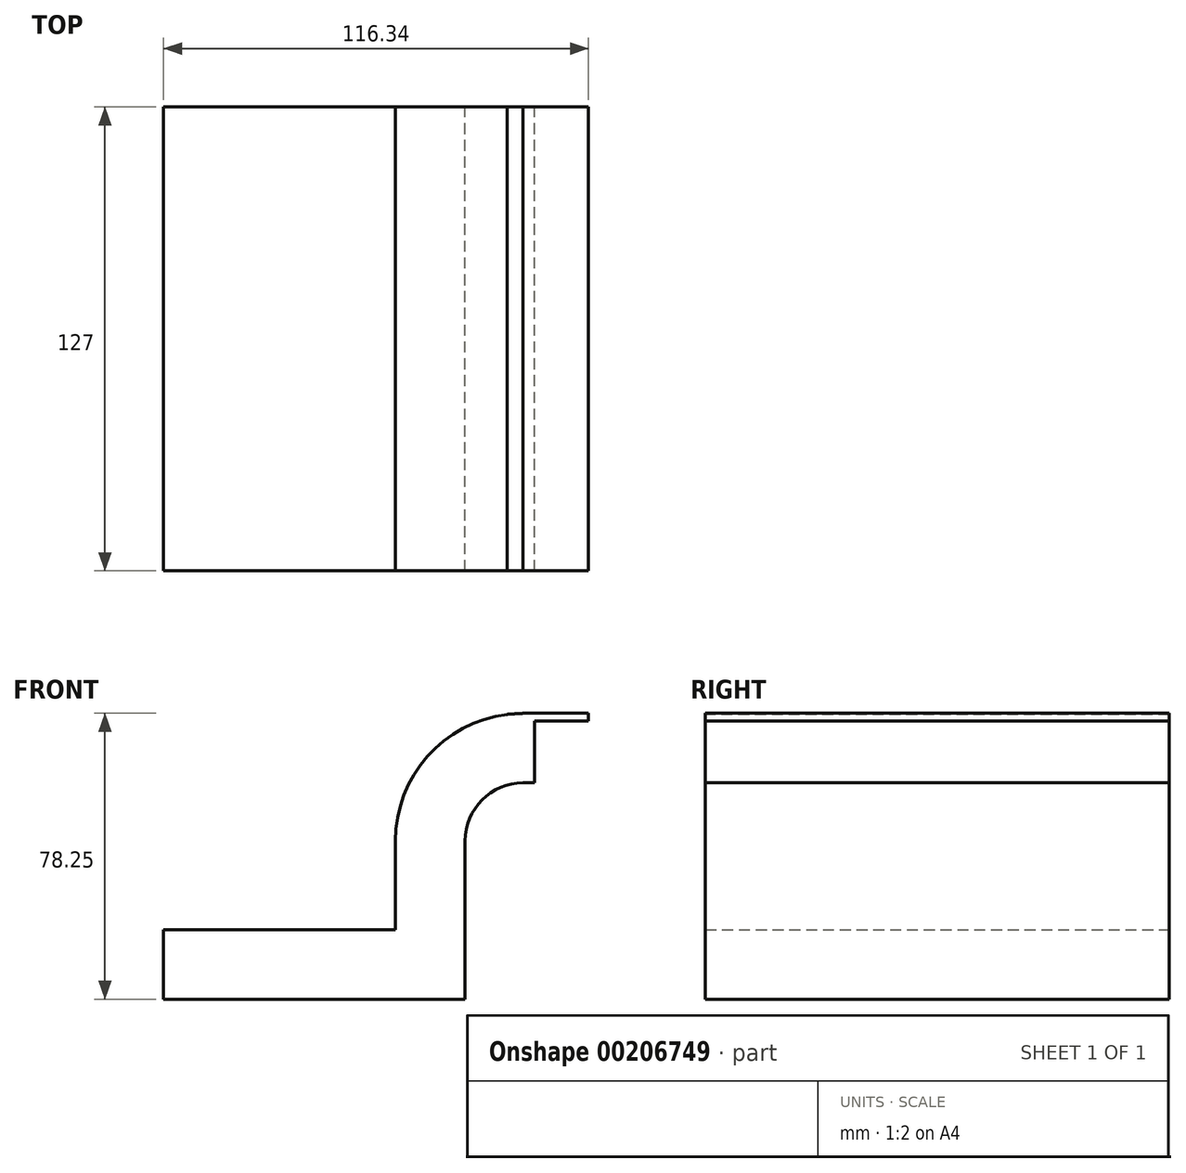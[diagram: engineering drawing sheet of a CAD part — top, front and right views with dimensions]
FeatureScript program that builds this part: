
annotation { "Feature Type Name" : "Feature", "Feature Type Description" : "" }
export const myFeature = defineFeature(function(context is Context, id is Id, definition is map)
    precondition{}
    {
        {
            var Q0;
            Q0=qCreatedBy(makeId("Front.planeOp"),FACE);
            var sketch = newSketch(context, id + "F0", { "sketchPlane" : qUnion([Q0])});
            skLineSegment(sketch, "E0.bottom", {"start": v(-41.28, -9.53) * mm, "end": v(41.28, -9.53) * mm});
            skLineSegment(sketch, "E0.top", {"start": v(-41.28, 9.53) * mm, "end": v(41.28, 9.53) * mm});
            skLineSegment(sketch, "E0.left", {"start": v(-41.28, -9.53) * mm, "end": v(-41.28, 9.53) * mm});
            skLineSegment(sketch, "E0.right", {"start": v(41.28, -9.53) * mm, "end": v(41.28, 9.52) * mm});
            skPoint(sketch, "E0.middle", {"position": v(0, 0) * mm});
            skLineSegment(sketch, "E1.bottom", {"start": v(111.12, 38.1) * mm, "end": v(60.32, 38.1) * mm});
            skLineSegment(sketch, "E1.top", {"start": v(111.12, 66.68) * mm, "end": v(60.32, 66.68) * mm});
            skLineSegment(sketch, "E1.left", {"start": v(111.12, 38.1) * mm, "end": v(111.12, 66.68) * mm});
            skLineSegment(sketch, "E1.right", {"start": v(60.32, 38.1) * mm, "end": v(60.32, 66.68) * mm});
            skPoint(sketch, "E1.middle", {"position": v(85.72, 52.39) * mm});
            skLineSegment(sketch, "E2", {"start": v(41.28, 9.52) * mm, "end": v(41.28, 33.8) * mm});
            skArc(sketch, "E3", {"start": v(41.27, 33.8) * mm, "mid": v(45.92, 45.02) * mm, "end": v(57.15, 49.67) * mm});
            skLineSegment(sketch, "E4", {"start": v(57.15, 49.67) * mm, "end": v(75.07, 49.67) * mm});
            skLineSegment(sketch, "E5.0", {"start": v(57.15, 68.72) * mm, "end": v(75.07, 68.72) * mm});
            skArc(sketch, "E5.1", {"start": v(22.22, 33.8) * mm, "mid": v(32.45, 58.5) * mm, "end": v(57.15, 68.72) * mm});
            skLineSegment(sketch, "E5.2", {"start": v(22.22, 9.52) * mm, "end": v(22.22, 33.8) * mm});
            skLineSegment(sketch, "E6", {"start": v(75.07, 49.67) * mm, "end": v(75.07, 68.72) * mm});
            skFitSpline(sketch, "E7", {"points": [v(57.15, 68.72) * mm, v(-41.28, 9.52) * mm], "startDerivative": vector(-206.41, -10.52) * mm, "endDerivative": vector(-98.42, -59.2) * mm});
            skFitSpline(sketch, "E8", {"points": [v(-8.47, 29.26) * mm, v(-26.45, 33.84) * mm], "startDerivative": vector(-17.98, 4.58) * mm, "endDerivative": vector(-17.98, 4.58) * mm});
            skSolve(sketch);
        }
        {
            var Q0;
            Q0=makeQuery(id+"F0.imprint","IMPRINT",FACE,{"disambiguationData":[TD([[makeQuery(id+"F0.imprint","IMPRINT",EDGE,{"derivedFrom":sQuery(id+"F0.wireOp",EDGE,"E0.bottom")}),1.0]])]});
            var Q1;
            {var subQ12=sQuery(id+"F0.wireOp",EDGE,"E2");Q1=makeQuery(id+"F0.imprint","IMPRINT",FACE,{"disambiguationData":[TD([[makeQuery(id+"F0.imprint","IMPRINT",EDGE,{"derivedFrom":subQ12}),1.0]])]});}
            extrude(context, id + "F1", {"entities" : qUnion([Q0, Q1]), "endBound" : BoundingType.SYMMETRIC, "depth" : 127 * mm});
        }
    });
